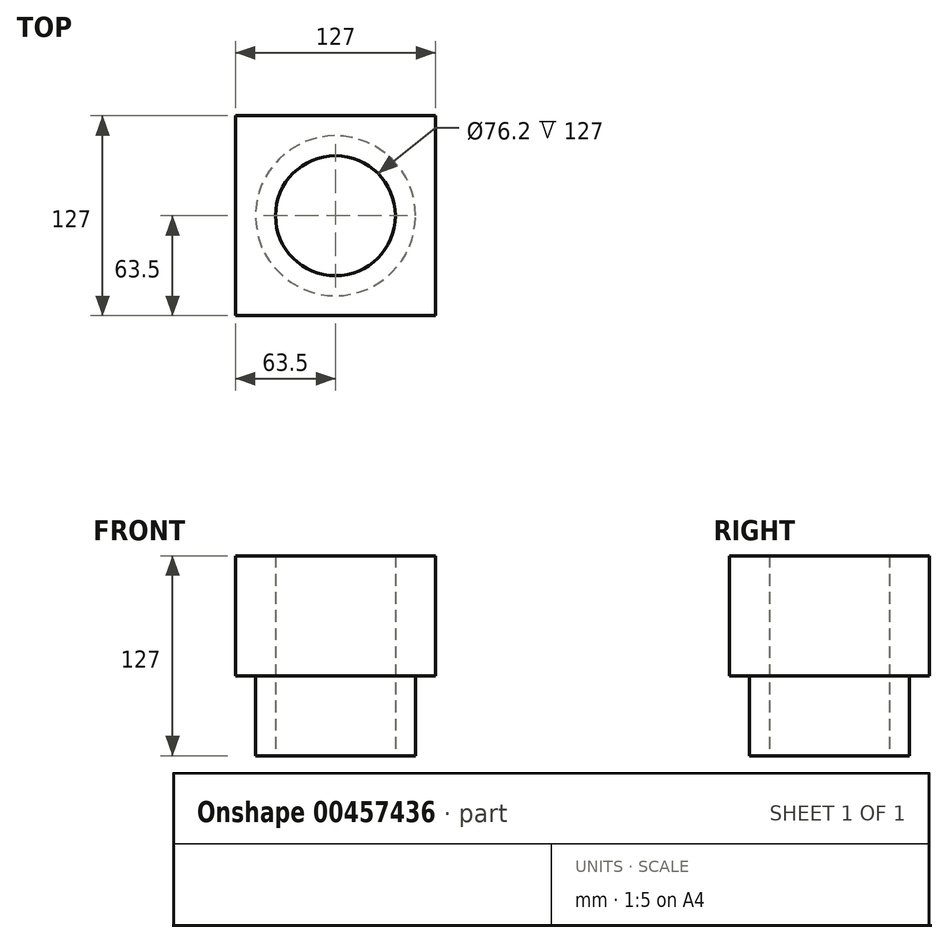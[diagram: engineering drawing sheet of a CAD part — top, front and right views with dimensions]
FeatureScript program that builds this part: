
annotation { "Feature Type Name" : "Feature", "Feature Type Description" : "" }
export const myFeature = defineFeature(function(context is Context, id is Id, definition is map)
    precondition{}
    {
        {
            var Q0;
            Q0=qCreatedBy(makeId("Top.planeOp"),FACE);
            var sketch = newSketch(context, id + "F0", { "sketchPlane" : qUnion([Q0])});
            skLineSegment(sketch, "E0.bottom", {"start": v(-63.5, 63.5) * mm, "end": v(63.5, 63.5) * mm});
            skLineSegment(sketch, "E0.top", {"start": v(-63.5, -63.5) * mm, "end": v(63.5, -63.5) * mm});
            skLineSegment(sketch, "E0.left", {"start": v(-63.5, 63.5) * mm, "end": v(-63.5, -63.5) * mm});
            skLineSegment(sketch, "E0.right", {"start": v(63.5, 63.5) * mm, "end": v(63.5, -63.5) * mm});
            skSolve(sketch);
        }
        {
            var Q0;
            Q0 = qSketchRegion(id + "F0", true);
            extrude(context, id + "F1", {"entities" : qUnion([Q0]), "endBound" : BoundingType.SYMMETRIC, "depth" : 76.2 * mm});
        }
        {
            var Q0;
            Q0=makeQuery(id+"F1.opExtrude","CAP_FACE",FACE,{"disambiguationData":[OSD([sQuery(id+"F0.wireOp",EDGE,"E0.bottom"),sQuery(id+"F0.wireOp",EDGE,"E0.top"),sQuery(id+"F0.wireOp",EDGE,"E0.left"),sQuery(id+"F0.wireOp",EDGE,"E0.right")])],"isStart":true});
            var sketch = newSketch(context, id + "F2", { "sketchPlane" : qUnion([Q0])});
            skCircle(sketch, "E1", {"center": v(0, 0) * mm, "radius": 50.8 * mm});
            skSolve(sketch);
        }
        {
            var Q0;
            Q0 = qSketchRegion(id + "F2", true);
            extrude(context, id + "F3", {"entities" : qUnion([Q0]), "operationType" : NewBodyOperationType.ADD, "depth" : 50.8 * mm});
        }
        {
            var Q0;
            Q0=makeQuery(id+"F3.opExtrude","CAP_FACE",FACE,{"disambiguationData":[OSD([sQuery(id+"F2.wireOp",EDGE,"E1")])],"isStart":false});
            var sketch = newSketch(context, id + "F4", { "sketchPlane" : qUnion([Q0])});
            skCircle(sketch, "E2", {"center": v(0, 0) * mm, "radius": 38.1 * mm});
            skSolve(sketch);
        }
        {
            var Q0;
            Q0 = qSketchRegion(id + "F4", true);
            extrude(context, id + "F5", {"entities" : qUnion([Q0]), "operationType" : NewBodyOperationType.REMOVE, "endBound" : BoundingType.THROUGH_ALL, "oppositeDirection" : true, "depth" : 25.4 * mm});
        }
    });
